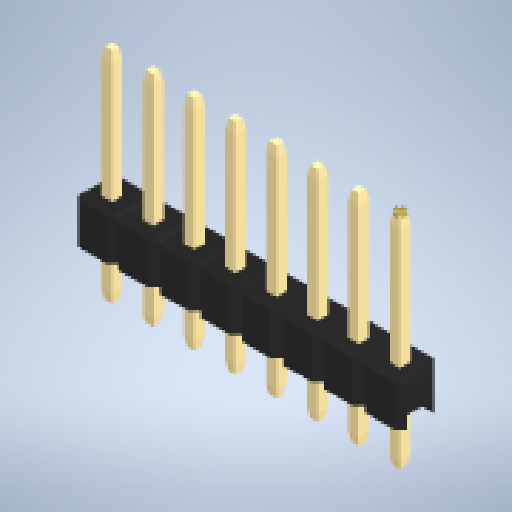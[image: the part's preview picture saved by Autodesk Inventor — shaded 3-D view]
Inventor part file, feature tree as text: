
AUTODESK INVENTOR PART (.ipt)
format: ipt  version: 2023.1 (Build 271208000, 208)  size: 339,456 bytes
history: native  units: in
note: dims shown in document units (in); Inventor stores cm internally (conversion verified against a paired STEP export)
features: other x10, chamfer x1, boolean_combine x1
ambient origin geometry x8: Origin, YZ Plane, XZ Plane, XY Plane, X Axis, Y Axis, Z Axis, Center Point
bodies: Solid1 (feature_tree), Solid2 (feature_tree), Solid3 (feature_tree), Solid4 (feature_tree), Solid5 (feature_tree), Solid6 (feature_tree), Solid7 (feature_tree), Solid8 (feature_tree), Solid9 (feature_tree)
feature tree (12):
  other  "Work Axis1"
  other  "Work Axis2"
  other  "Work Point5"
  chamfer  "Chamfer3"  [1 undecoded]
  other  "LPattern1[1]"
  other  "LPattern1[2]"
  other  "LPattern1[3]"
  other  "LPattern1[4]"
  other  "LPattern1[5]"
  other  "LPattern1[6]"
  other  "LPattern1[7]"
  boolean_combine  "Combine1"
note: 1 required parameter value undecoded (feature->parameter linkage not recoverable at this tier; creation-order binding heuristic only, values carry confidence <= 0.55)
